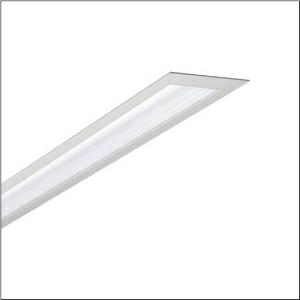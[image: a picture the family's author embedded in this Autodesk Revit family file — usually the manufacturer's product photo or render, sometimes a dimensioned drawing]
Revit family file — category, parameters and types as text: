
# Revit family: silica_r_5mx11bd2w4a_6c5b
name_source: partatom
category: Lighting Fixtures
units: mm (PartAtom-declared; Revit-internal decimal feet)

## family parameters
Cut with Voids When Loaded = No
Host = Face
Light Source = No
Part Type = Normal
Room Calculation Point = No
Round Connector Dimension = Use Diameter
Shared = No

## types (1)
- --- (1 x LED, 9910 lm, 60.1 W, 4000K)
    Apparent Load = 60 VA
    CIE Flux Codes = 82 97 100 100 100
    Color Rendering = 80
    Color Temperature = 4000K
    Default Elevation = 1800 mm
    Description = Silica®, office luminaire, of aluminium, light emission: direct distribution, primary light characteristic: symmetric, installation type: recessed, LED rated luminous flux: 9.910 lm, light colour: 840, colour temperature: 4000K, control gear: ECG DALI, with terminal, 3+2-pole, max. 2.5mm², mains connection: 230V, AC, 50/60Hz, rated input power: 60W, luminaire housing, of aluminium, matt pure white (RAL 9010), length: 2.864 mm, width: 93 mm, height: 60mm, end cap, of diecast zinc, pure white (RAL 9010), protection rating (complete): IP20, insulation class (complete): insulation class I (protective earthing), certification: CE, permissible ambient temperature for indoor applications: 0..+35°C, standard: EN 50419, packaging unit: 1 piece
    Height = 0 mm  [stored 0 ft]
    Lamp = 1 x LED
    Lamp Light Flux = 9910 lm
    Lamp Power = 60.1 W
    Lamp count = 1
    Length = 2865 mm
    Luminous efficacy = 165 lm/W
    Manufacturer = Siteco
    ModVariant = No
    Model = 5MX11BD2W4A
    Mounting Place = Ceiling
    Mounting Type = Recessed
    Number of Poles = 1
    OnlyDefault = Yes
    Power Factor = 1
    Product Name = Silica®
    Product group = office luminaire | ceiling recessed
    ProductGroupID = 400
    Protection Class = Protection class I
    Protection Degree = IP 20
    RLX_Detail_Level = 1
    RlxData = <blob elided: 24341 chars, md5=54d35883>
    Socket = socket
    Standby Power = 0 W
    System Light Flux = 9910 lm
    System Power = 60 W
    Type Comments = factory setting: luminous flux: 100 % | dim-lin: 254 | 336 mA
    Type Image = l_1004825.jpg
    URL = http://relux.com
    VarID = @adj_132022
    Voltage = 0 V
    Weight = 0.00 kg
    Width = 93 mm

note: [stored X ft] marks values corroborated as IEEE doubles in the binary element streams (Revit-internal decimal feet)

## geometry (parser evidence)
native form markers: Blend x4, Sweep x11
no freeform markers — native parametric forms only
